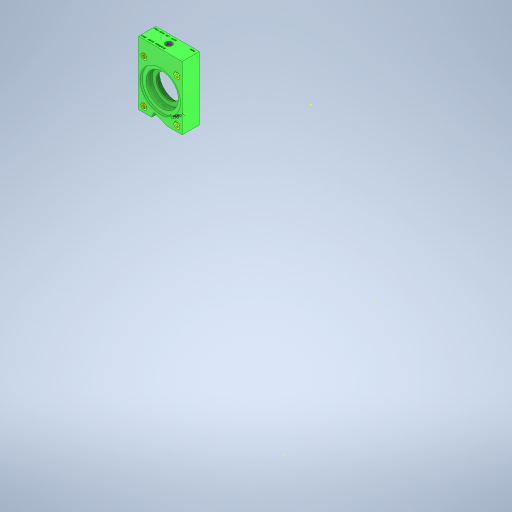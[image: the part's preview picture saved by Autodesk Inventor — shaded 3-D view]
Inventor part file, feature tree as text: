
AUTODESK INVENTOR PART (.ipt)
format: ipt  version: 2024.1 (Build 281209000, 209)  size: 924,160 bytes
history: native  units: in
note: dims shown in document units (in); Inventor stores cm internally (conversion verified against a paired STEP export)
features: hole x7, extrude x5, sketch x4, fillet x1
ambient origin geometry x8: Origin, YZ Plane, XZ Plane, XY Plane, X Axis, Y Axis, Z Axis, Center Point
bodies: Solid1 (feature_tree)
feature tree (17):
  extrude  "Extrusion1"  Depth=0.4in TaperAngle=0.0deg
  extrude  "Extrusion2"  Depth=0.0312in
  extrude  "Extrusion3"  Depth=0.0312in
  hole  "Hole1"  [1 undecoded]
  hole  "Hole2"  [1 undecoded]
  extrude  "Extrusion4"  Depth=0.0312in
  hole  "Hole5"  [1 undecoded]
  hole  "Hole6"  [1 undecoded]
  fillet  "Fillet1"  Radius=1.0in
  sketch  "Sketch7"  dims[d13=0.03in d14=0.75in d15=0.507in d16=0.25in d17=0.5635in d18=1.0in d19=0.8108in d20=0.4583in d21=0.29in d22=0.04in d23=0.75in d24=0.507in d25=0.25in d26=0.5635in d27=1.0in d28=0.8108in d29=0.213in d30=0.75in d31=0.507in d32=0.25in d33=0.5635in d34=0.25in d35=0.0in d36=0.75in d38=135.0deg d39=0.4583in d40=112.5deg d41=0.25in d42=1.0in d43=0.0in d44=0.29in d45=0.196in d46=0.211in d47=0.22in d48=0.375in d49=0.25in d50=0.5635in d51=0.22in d52=0.0in d53=0.03in d54=0.75in d55=0.375in d56=0.25in d57=0.5635in d58=0.6in d59=0.8108in d60=0.0312in d61=0.13in d62=1.0in d63=0.375in d64=0.25in d65=0.5635in d66=1.0in d67=0.8108in d68=1.0in d69=0.0in]
  extrude  "Extrusion5"  Depth=0.0312in
  hole  "Hole7"  [1 undecoded]
  hole  "Hole3"  [1 undecoded]
  hole  "Hole4"  [1 undecoded]
  sketch  "Sketch1"  dims[d0=0.5in d1=0.0in d2=0.4in d3=0.0in]
  sketch  "Sketch2"  dims[d4=0.6in d5=0.0in]
  sketch  "Sketch5"  dims[d6=0.211in d7=0.25in d8=0.507in d9=0.25in d10=0.5635in d11=0.25in d12=0.0in]
note: 7 required parameter values undecoded (feature->parameter linkage not recoverable at this tier; creation-order binding heuristic only, values carry confidence <= 0.55)
